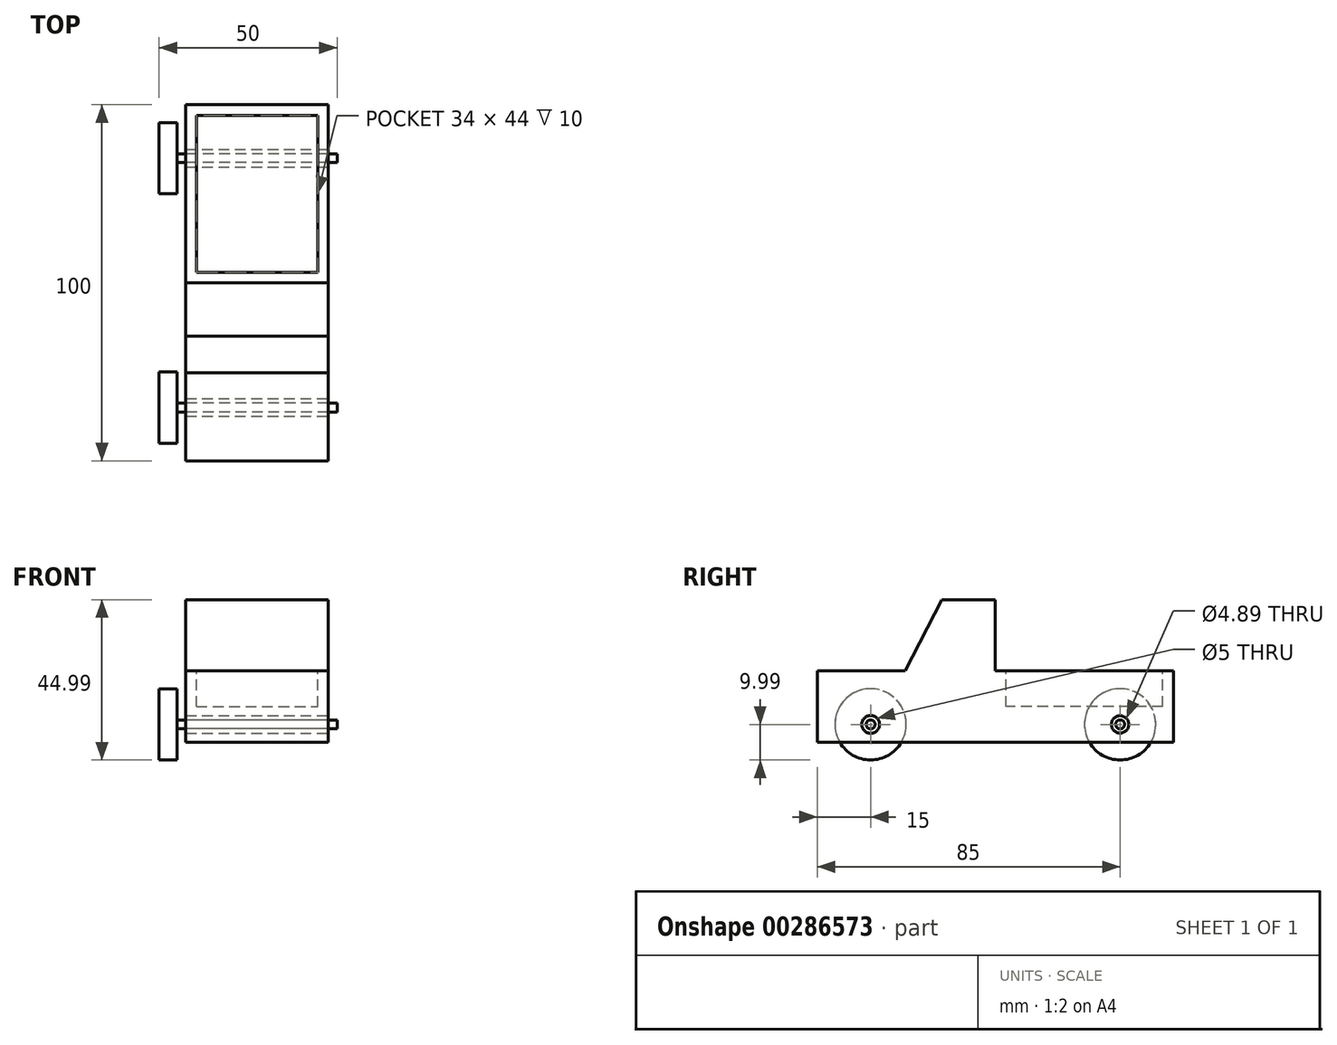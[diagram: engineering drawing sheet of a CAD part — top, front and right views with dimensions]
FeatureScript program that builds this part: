
annotation { "Feature Type Name" : "Feature", "Feature Type Description" : "" }
export const myFeature = defineFeature(function(context is Context, id is Id, definition is map)
    precondition{}
    {
        {
            var Q0;
            Q0=qCreatedBy(makeId("Right.planeOp"),FACE);
            var sketch = newSketch(context, id + "F0", { "sketchPlane" : qUnion([Q0])});
            skLineSegment(sketch, "E0.bottom", {"start": v(-50, 10) * mm, "end": v(50, 10) * mm});
            skLineSegment(sketch, "E0.top", {"start": v(-50, -10) * mm, "end": v(50, -10) * mm});
            skLineSegment(sketch, "E0.left", {"start": v(-50, 10) * mm, "end": v(-50, -10) * mm});
            skLineSegment(sketch, "E0.right", {"start": v(50, 10) * mm, "end": v(50, -10) * mm});
            skPoint(sketch, "E0.middle", {"position": v(0, 0) * mm});
            skSolve(sketch);
        }
        {
            var Q0;
            Q0 = qSketchRegion(id + "F0", true);
            extrude(context, id + "F1", {"entities" : qUnion([Q0]), "depth" : 40 * mm});
        }
        {
            var Q0;
            Q0=makeQuery(id+"F1.opExtrude","CAP_FACE",FACE,{"disambiguationData":[OSD([sQuery(id+"F0.wireOp",EDGE,"E0.bottom"),sQuery(id+"F0.wireOp",EDGE,"E0.top"),sQuery(id+"F0.wireOp",EDGE,"E0.left"),sQuery(id+"F0.wireOp",EDGE,"E0.right")])],"isStart":false});
            var sketch = newSketch(context, id + "F2", { "sketchPlane" : qUnion([Q0])});
            skLineSegment(sketch, "E1", {"start": v(0, 10) * mm, "end": v(0, 30) * mm});
            skPoint(sketch, "E1.endSnap0", {"position": v(0, 10) * mm});
            skLineSegment(sketch, "E2", {"start": v(0, 30) * mm, "end": v(-15, 30) * mm});
            skLineSegment(sketch, "E3", {"start": v(-15, 30) * mm, "end": v(-25.3, 10) * mm});
            skSolve(sketch);
        }
        {
            var Q0;
            Q0=makeQuery(id+"F1.opExtrude","CAP_FACE",FACE,{"disambiguationData":[OSD([sQuery(id+"F0.wireOp",EDGE,"E0.bottom"),sQuery(id+"F0.wireOp",EDGE,"E0.top"),sQuery(id+"F0.wireOp",EDGE,"E0.left"),sQuery(id+"F0.wireOp",EDGE,"E0.right")])],"isStart":true});
            var sketch = newSketch(context, id + "F3", { "sketchPlane" : qUnion([Q0])});
            skLineSegment(sketch, "E4", {"start": v(0, 10) * mm, "end": v(0, 30) * mm});
            skPoint(sketch, "E4.endSnap0", {"position": v(0, 10) * mm});
            skLineSegment(sketch, "E5", {"start": v(0, 30) * mm, "end": v(15, 30) * mm});
            skLineSegment(sketch, "E6", {"start": v(15, 30) * mm, "end": v(25.3, 10) * mm});
            skSolve(sketch);
        }
        {
            var Q1;
            {var subQ0=sQuery(id+"F3.wireOp",EDGE,"E4");Q1=makeQuery(id+"F3.imprint","IMPRINT",FACE,{"disambiguationData":[TD([[makeQuery(id+"F3.imprint","IMPRINT",EDGE,{"derivedFrom":subQ0}),-1.0]])]});}
            var Q2;
            {var subQ0=sQuery(id+"F2.wireOp",EDGE,"E1");Q2=makeQuery(id+"F2.imprint","IMPRINT",FACE,{"disambiguationData":[TD([[makeQuery(id+"F2.imprint","IMPRINT",EDGE,{"derivedFrom":subQ0}),1.0]])]});}
            loft(context, id + "F4", {"operationType" : NewBodyOperationType.ADD, "sheetProfilesArray" : [{ "sheetProfileEntities" : qUnion([Q1]) }, { "sheetProfileEntities" : qUnion([Q2]) }]});
        }
        {
            var Q0;
            {var subQ0=sQuery(id+"F2.wireOp",EDGE,"E1");var subQ2=sQuery(id+"F0.wireOp",EDGE,"E0.bottom");Q0=makeQuery(id+"F4.boolean.opBoolean","MERGE",FACE,{"derivedFrom":[makeQuery(id+"F1.opExtrude","CAP_FACE",FACE,{"disambiguationData":[OSD([subQ2,sQuery(id+"F0.wireOp",EDGE,"E0.top"),sQuery(id+"F0.wireOp",EDGE,"E0.left"),sQuery(id+"F0.wireOp",EDGE,"E0.right")])],"isStart":false}),makeQuery(id+"F4.opLoft","CAP_FACE",FACE,{"disambiguationData":[OSD([makeQuery(id+"F2.imprint","IMPRINT",FACE,{"disambiguationData":[TD([[makeQuery(id+"F2.imprint","IMPRINT",EDGE,{"derivedFrom":subQ0}),1.0]])]})])],"isStart":true})]});}
            var sketch = newSketch(context, id + "F5", { "sketchPlane" : qUnion([Q0])});
            skCircle(sketch, "E7", {"center": v(-35, -5) * mm, "radius": 2.5 * mm});
            skCircle(sketch, "E8", {"center": v(35, -5) * mm, "radius": 2.44 * mm});
            skSolve(sketch);
        }
        {
            var Q0;
            Q0=makeQuery(id+"F5.imprint","IMPRINT",FACE,{"disambiguationData":[TD([[makeQuery(id+"F5.imprint","IMPRINT",EDGE,{"derivedFrom":sQuery(id+"F5.wireOp",EDGE,"E7")}),1.0]])]});
            var Q1;
            Q1=makeQuery(id+"F5.imprint","IMPRINT",FACE,{"disambiguationData":[TD([[makeQuery(id+"F5.imprint","IMPRINT",EDGE,{"derivedFrom":sQuery(id+"F5.wireOp",EDGE,"E8")}),1.0]])]});
            extrude(context, id + "F6", {"entities" : qUnion([Q0, Q1]), "operationType" : NewBodyOperationType.REMOVE, "endBound" : BoundingType.THROUGH_ALL, "oppositeDirection" : true, "depth" : 25 * mm});
        }
        {
            var Q0;
            {var subQ4=sQuery(id+"F0.wireOp",EDGE,"E0.bottom");var subQ5=sQuery(id+"F0.wireOp",EDGE,"E0.right");Q0=makeQuery(id+"F4.boolean.opBoolean","SPLIT",FACE,{"disambiguationData":[TD([makeQuery(id+"F1.opExtrude","SWEPT_FACE",FACE,{"disambiguationData":[OSD([subQ5])]})])],"derivedFrom":makeQuery(id+"F1.opExtrude","SWEPT_FACE",FACE,{"disambiguationData":[OSD([subQ4])]})});}
            var sketch = newSketch(context, id + "F7", { "sketchPlane" : qUnion([Q0])});
            skLineSegment(sketch, "E9.bottom", {"start": v(3, 47) * mm, "end": v(37, 47) * mm});
            skLineSegment(sketch, "E9.top", {"start": v(3, 3) * mm, "end": v(37, 3) * mm});
            skLineSegment(sketch, "E9.left", {"start": v(3, 47) * mm, "end": v(3, 3) * mm});
            skLineSegment(sketch, "E9.right", {"start": v(37, 47) * mm, "end": v(37, 3) * mm});
            skSolve(sketch);
        }
        {
            var Q0;
            Q0=makeQuery(id+"F7.imprint","IMPRINT",FACE,{"disambiguationData":[TD([[makeQuery(id+"F7.imprint","IMPRINT",EDGE,{"derivedFrom":sQuery(id+"F7.wireOp",EDGE,"E9.bottom")}),-1.0]])]});
            extrude(context, id + "F8", {"entities" : qUnion([Q0]), "operationType" : NewBodyOperationType.REMOVE, "oppositeDirection" : true, "depth" : 10 * mm});
        }
        {
            var Q0;
            Q0=qCreatedBy(makeId("Right.planeOp"),FACE);
            var sketch = newSketch(context, id + "F9", { "sketchPlane" : qUnion([Q0])});
            skCircle(sketch, "E10", {"center": v(35.01, -5) * mm, "radius": 1.26 * mm});
            skPoint(sketch, "E10.first.point", {"position": v(36.01, -4.23) * mm});
            skPoint(sketch, "E10.second.point", {"position": v(33.79, -4.7) * mm});
            skPoint(sketch, "E10.third.point", {"position": v(35.04, -6.25) * mm});
            skSolve(sketch);
        }
        {
            var Q0;
            Q0 = qSketchRegion(id + "F9", true);
            extrude(context, id + "F10", {"entities" : qUnion([Q0]), "depth" : 42.5 * mm});
        }
        {
            var Q0;
            Q0=makeQuery(id+"F9.imprint","IMPRINT",FACE,{"disambiguationData":[TD([[makeQuery(id+"F9.imprint","IMPRINT",EDGE,{"derivedFrom":sQuery(id+"F9.wireOp",EDGE,"E10")}),1.0]])]});
            extrude(context, id + "F11", {"entities" : qUnion([Q0]), "operationType" : NewBodyOperationType.ADD, "oppositeDirection" : true, "depth" : 2.5 * mm});
        }
        {
            var Q0;
            Q0=makeQuery(id+"F11.opExtrude","CAP_FACE",FACE,{"disambiguationData":[OSD([sQuery(id+"F9.wireOp",EDGE,"E10")])],"isStart":false});
            var sketch = newSketch(context, id + "F12", { "sketchPlane" : qUnion([Q0])});
            skCircle(sketch, "E11", {"center": v(-35.01, -5) * mm, "radius": 10 * mm});
            skSolve(sketch);
        }
        {
            var Q0;
            Q0 = qSketchRegion(id + "F12", true);
            extrude(context, id + "F13", {"entities" : qUnion([Q0]), "depth" : 5 * mm});
        }
        {
            var Q0;
            Q0=makeQuery(id+"F13.opExtrude","SWEPT_BODY",BODY,{"disambiguationData":[OSD([sQuery(id+"F12.wireOp",EDGE,"E11")])]});
            var Q1;
            Q1=makeQuery(id+"F10.opExtrude","SWEPT_BODY",BODY,{"disambiguationData":[OSD([sQuery(id+"F9.wireOp",EDGE,"E10")])]});
            var Q2;
            Q2=qCreatedBy(makeId("Front.planeOp"),FACE);
            mirror(context, id + "F14", {"operationType" : NewBodyOperationType.ADD, "entities" : qUnion([Q0, Q1]), "mirrorPlane" : qUnion([Q2])});
        }
        {
            var Q0;
            Q0=makeQuery(id+"F10.opExtrude","CAP_FACE",FACE,{"disambiguationData":[OSD([sQuery(id+"F9.wireOp",EDGE,"E10")])],"isStart":false});
            var sketch = newSketch(context, id + "F15", { "sketchPlane" : qUnion([Q0])});
            skCircle(sketch, "E12", {"center": v(35.01, -5) * mm, "radius": 10 * mm});
            skSolve(sketch);
        }
        {
            var Q0;
            Q0=sQuery(id+"F15.wireOp",EDGE,"E12");
            extrude(context, id + "F16", {"bodyType" : ToolBodyType.SURFACE, "surfaceEntities" : qUnion([Q0]), "depth" : 5 * mm});
        }
        {
            var Q0;
            Q0=makeQuery(id+"F16.opExtrude","SWEPT_BODY",BODY,{"disambiguationData":[OSD([sQuery(id+"F15.wireOp",EDGE,"E12")])]});
            var Q1;
            Q1=qCreatedBy(makeId("Front.planeOp"),FACE);
            mirror(context, id + "F17", {"entities" : qUnion([Q0]), "mirrorPlane" : qUnion([Q1])});
        }
    });
